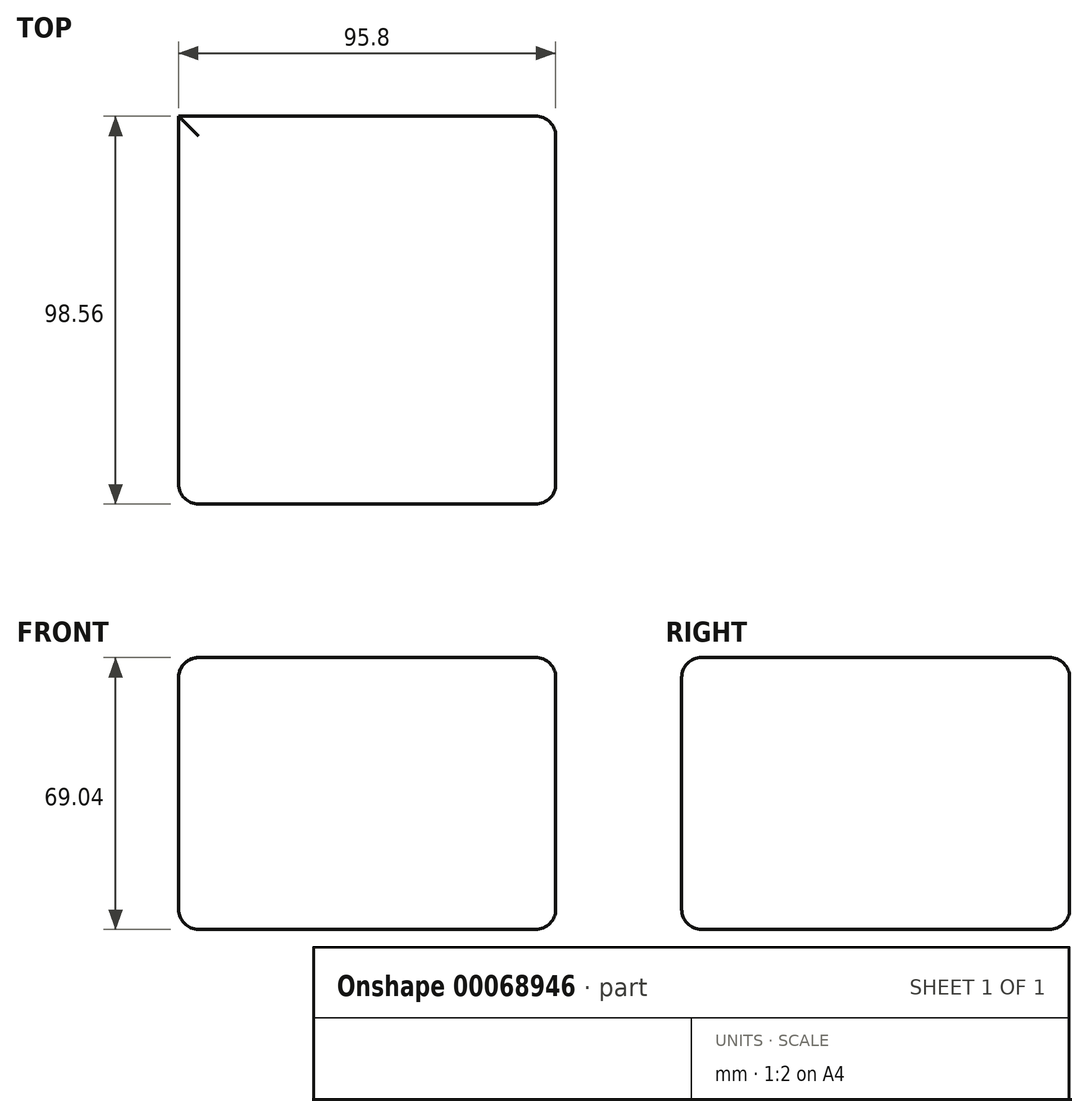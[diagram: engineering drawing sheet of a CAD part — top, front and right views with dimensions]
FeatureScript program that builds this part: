
annotation { "Feature Type Name" : "Feature", "Feature Type Description" : "" }
export const myFeature = defineFeature(function(context is Context, id is Id, definition is map)
    precondition{}
    {
        {
            var Q0;
            Q0=qCreatedBy(makeId("Top.planeOp"),FACE);
            var sketch = newSketch(context, id + "F0", { "sketchPlane" : qUnion([Q0])});
            skLineSegment(sketch, "E0.bottom", {"start": v(95.8, 0) * mm, "end": v(0, 0) * mm});
            skLineSegment(sketch, "E0.top", {"start": v(95.8, 98.56) * mm, "end": v(0, 98.56) * mm});
            skLineSegment(sketch, "E0.left", {"start": v(95.8, 0) * mm, "end": v(95.8, 98.56) * mm});
            skLineSegment(sketch, "E0.right", {"start": v(0, 0) * mm, "end": v(0, 98.56) * mm});
            skSolve(sketch);
        }
        {
            var Q0;
            Q0=makeQuery(id+"F0.imprint","IMPRINT",FACE,{"disambiguationData":[TD([[makeQuery(id+"F0.imprint","IMPRINT",EDGE,{"derivedFrom":sQuery(id+"F0.wireOp",EDGE,"E0.bottom")}),-1.0]])]});
            extrude(context, id + "F1", {"entities" : qUnion([Q0]), "depth" : 69.04 * mm});
        }
        {
            var Q0;
            Q0=makeQuery(id+"F1.opExtrude","CAP_FACE",FACE,{"disambiguationData":[OSD([sQuery(id+"F0.wireOp",EDGE,"E0.bottom"),sQuery(id+"F0.wireOp",EDGE,"E0.top"),sQuery(id+"F0.wireOp",EDGE,"E0.left"),sQuery(id+"F0.wireOp",EDGE,"E0.right")])],"isStart":false});
            var Q1;
            Q1=makeQuery(id+"F1.opExtrude","SWEPT_EDGE",EDGE,{"disambiguationData":[OSD([sQuery(id+"F0.wireOp",EDGE,"E0.bottom"),sQuery(id+"F0.wireOp",EDGE,"E0.left")])]});
            var Q2;
            Q2=makeQuery(id+"F1.opExtrude","SWEPT_EDGE",EDGE,{"disambiguationData":[OSD([sQuery(id+"F0.wireOp",EDGE,"E0.bottom"),sQuery(id+"F0.wireOp",EDGE,"E0.right")])]});
            var Q3;
            Q3=makeQuery(id+"F1.opExtrude","SWEPT_EDGE",EDGE,{"disambiguationData":[OSD([sQuery(id+"F0.wireOp",EDGE,"E0.top"),sQuery(id+"F0.wireOp",EDGE,"E0.left")])]});
            var Q4;
            Q4=makeQuery(id+"F1.opExtrude","CAP_EDGE",EDGE,{"disambiguationData":[OSD([sQuery(id+"F0.wireOp",EDGE,"E0.bottom")])],"isStart":true});
            var Q5;
            Q5=makeQuery(id+"F1.opExtrude","CAP_EDGE",EDGE,{"disambiguationData":[OSD([sQuery(id+"F0.wireOp",EDGE,"E0.bottom")])],"isStart":false});
            var Q6;
            Q6=makeQuery(id+"F1.opExtrude","CAP_EDGE",EDGE,{"disambiguationData":[OSD([sQuery(id+"F0.wireOp",EDGE,"E0.left")])],"isStart":true});
            var Q7;
            Q7=makeQuery(id+"F1.opExtrude","CAP_EDGE",EDGE,{"disambiguationData":[OSD([sQuery(id+"F0.wireOp",EDGE,"E0.left")])],"isStart":false});
            var Q8;
            Q8=makeQuery(id+"F1.opExtrude","CAP_EDGE",EDGE,{"disambiguationData":[OSD([sQuery(id+"F0.wireOp",EDGE,"E0.top")])],"isStart":true});
            var Q9;
            Q9=makeQuery(id+"F1.opExtrude","CAP_EDGE",EDGE,{"disambiguationData":[OSD([sQuery(id+"F0.wireOp",EDGE,"E0.right")])],"isStart":true});
            fillet(context, id + "F2", {"entities" : qUnion([Q0, Q1, Q2, Q3, Q4, Q5, Q6, Q7, Q8, Q9]), "radius" : 5.08 * mm, "tangentPropagation" : true, "allowEdgeOverflow" : false});
        }
    });
